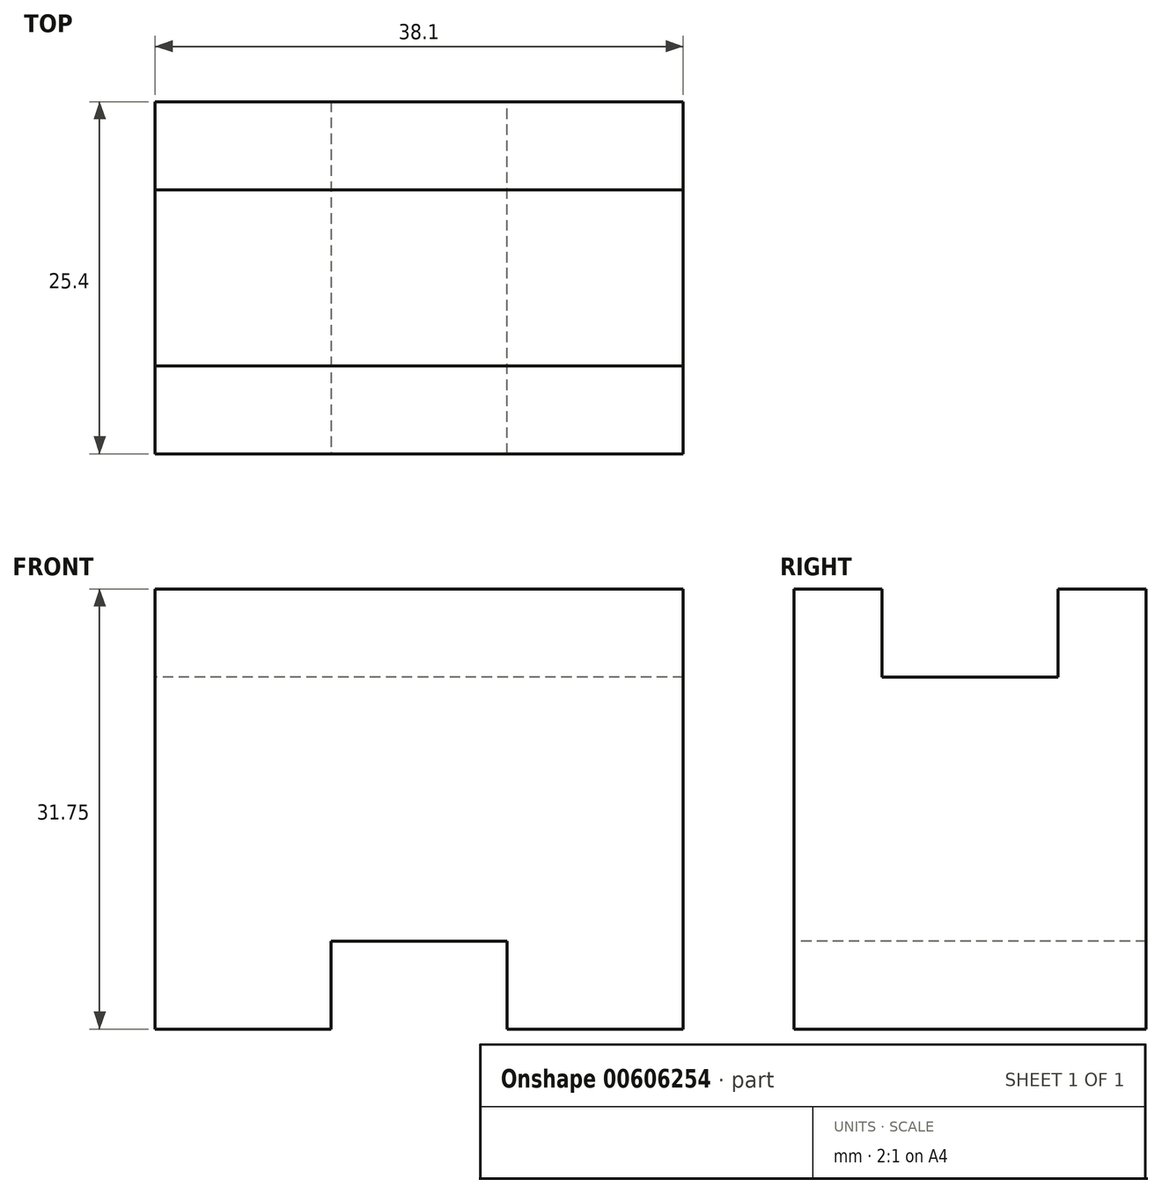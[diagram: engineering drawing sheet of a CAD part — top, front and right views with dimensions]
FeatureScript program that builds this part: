
annotation { "Feature Type Name" : "Feature", "Feature Type Description" : "" }
export const myFeature = defineFeature(function(context is Context, id is Id, definition is map)
    precondition{}
    {
        {
            var Q0;
            Q0=qCreatedBy(makeId("Right.planeOp"),FACE);
            var sketch = newSketch(context, id + "F0", { "sketchPlane" : qUnion([Q0])});
            skLineSegment(sketch, "E0", {"start": v(0, 0) * mm, "end": v(0, 6.35) * mm});
            skLineSegment(sketch, "E1", {"start": v(0, 6.35) * mm, "end": v(-6.35, 6.35) * mm});
            skLineSegment(sketch, "E2", {"start": v(-6.35, 6.35) * mm, "end": v(-6.35, -25.4) * mm});
            skLineSegment(sketch, "E3", {"start": v(-6.35, -25.4) * mm, "end": v(19.05, -25.4) * mm});
            skLineSegment(sketch, "E4", {"start": v(19.05, -25.4) * mm, "end": v(19.05, 6.35) * mm});
            skLineSegment(sketch, "E5", {"start": v(19.05, 6.35) * mm, "end": v(12.7, 6.35) * mm});
            skLineSegment(sketch, "E6", {"start": v(12.7, 6.35) * mm, "end": v(12.7, 0) * mm});
            skLineSegment(sketch, "E7", {"start": v(12.7, 0) * mm, "end": v(0, 0) * mm});
            skSolve(sketch);
        }
        {
            var Q0;
            Q0 = qSketchRegion(id + "F0", true);
            extrude(context, id + "F1", {"entities" : qUnion([Q0]), "depth" : 38.1 * mm, "offsetDistance" : 25.4 * mm});
        }
        {
            var Q0;
            Q0=makeQuery(id+"F1.opExtrude","SWEPT_FACE",FACE,{"disambiguationData":[OSD([sQuery(id+"F0.wireOp",EDGE,"E3")])]});
            var sketch = newSketch(context, id + "F2", { "sketchPlane" : qUnion([Q0])});
            skLineSegment(sketch, "E8", {"start": v(0, -19.05) * mm, "end": v(12.7, -19.05) * mm});
            skLineSegment(sketch, "E9", {"start": v(12.7, -19.05) * mm, "end": v(12.7, 6.35) * mm});
            skLineSegment(sketch, "E10", {"start": v(12.7, 6.35) * mm, "end": v(25.4, 6.35) * mm});
            skLineSegment(sketch, "E11", {"start": v(25.4, 6.35) * mm, "end": v(25.4, -19.05) * mm});
            skSolve(sketch);
        }
        {
            var Q0;
            {var subQ0=sQuery(id+"F2.wireOp",EDGE,"E9");Q0=makeQuery(id+"F2.imprint","IMPRINT",FACE,{"disambiguationData":[TD([[makeQuery(id+"F2.imprint","IMPRINT",EDGE,{"derivedFrom":subQ0}),-1.0]])]});}
            extrude(context, id + "F3", {"entities" : qUnion([Q0]), "operationType" : NewBodyOperationType.REMOVE, "oppositeDirection" : true, "depth" : 6.35 * mm, "offsetDistance" : 25.4 * mm});
        }
    });
